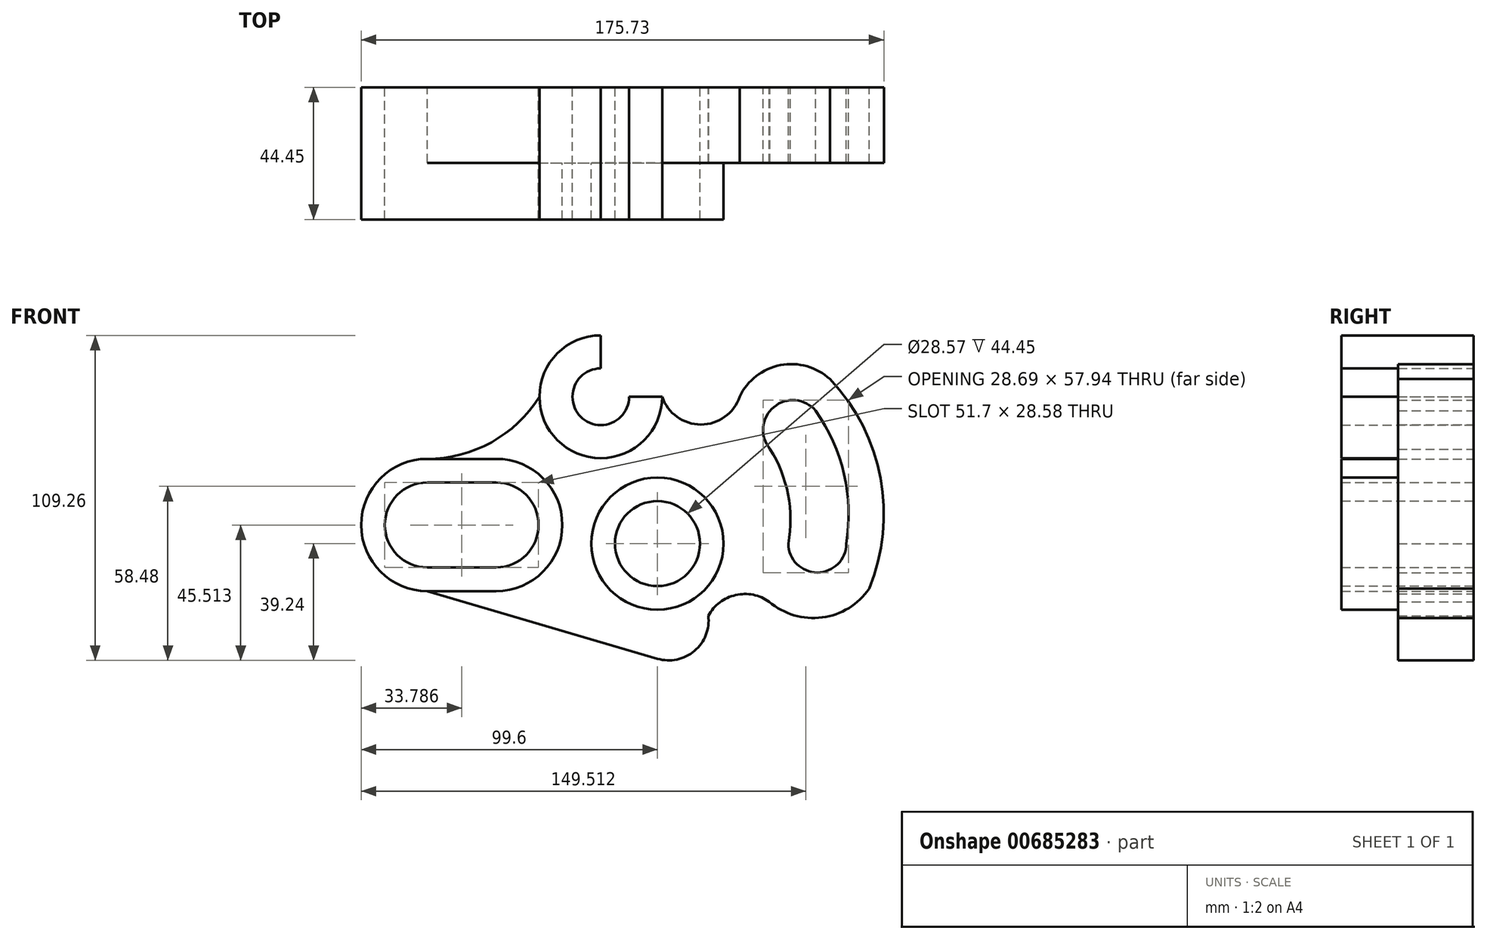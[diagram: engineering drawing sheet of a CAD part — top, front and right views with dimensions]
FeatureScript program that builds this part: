
annotation { "Feature Type Name" : "Feature", "Feature Type Description" : "" }
export const myFeature = defineFeature(function(context is Context, id is Id, definition is map)
    precondition{}
    {
        {
            var Q0;
            Q0=qCreatedBy(makeId("Front.planeOp"),FACE);
            var sketch = newSketch(context, id + "F0", { "sketchPlane" : qUnion([Q0])});
            skLineSegment(sketch, "E0", {"start": v(0, 0) * mm, "end": v(63.5, 0) * mm});
            skCircle(sketch, "E1", {"center": v(0, 0) * mm, "radius": 14.29 * mm});
            skCircle(sketch, "E2", {"center": v(0, 0) * mm, "radius": 22.23 * mm});
            skArc(sketch, "E3", {"start": v(-77.37, 28.5) * mm, "mid": v(-99.6, 6.27) * mm, "end": v(-77.37, -15.95) * mm});
            skLineSegment(sketch, "E4", {"start": v(-77.37, 28.5) * mm, "end": v(-54.2, 28.5) * mm});
            skLineSegment(sketch, "E5", {"start": v(-77.37, -15.95) * mm, "end": v(-54.2, -15.95) * mm});
            skArc(sketch, "E6", {"start": v(-54.2, -15.95) * mm, "mid": v(-31.98, 6.27) * mm, "end": v(-54.2, 28.5) * mm});
            skArc(sketch, "E7", {"start": v(-77.37, 20.56) * mm, "mid": v(-91.66, 6.27) * mm, "end": v(-77.37, -8.01) * mm});
            skArc(sketch, "E8", {"start": v(-54.2, -8.01) * mm, "mid": v(-39.97, 6.27) * mm, "end": v(-54.2, 20.56) * mm});
            skLineSegment(sketch, "E9", {"start": v(-77.37, 20.56) * mm, "end": v(-54.2, 20.56) * mm});
            skLineSegment(sketch, "E10", {"start": v(-77.37, -8.01) * mm, "end": v(-54.2, -8.01) * mm});
            skLineSegment(sketch, "E11", {"start": v(-77.37, -15.95) * mm, "end": v(0, -38.7) * mm});
            skCircle(sketch, "E12", {"center": v(-19.05, 49.38) * mm, "radius": 9.53 * mm});
            skCircle(sketch, "E13", {"center": v(-19.05, 49.38) * mm, "radius": 20.64 * mm});
            skLineSegment(sketch, "E14", {"start": v(-19.05, 87.42) * mm, "end": v(-19.05, 22.5) * mm});
            skArc(sketch, "E15", {"start": v(-77.37, 28.5) * mm, "mid": v(-55.83, 34.07) * mm, "end": v(-39.69, 49.38) * mm});
            skLineSegment(sketch, "E16", {"start": v(0, 0) * mm, "end": v(53.23, 44.67) * mm});
            skArc(sketch, "E17", {"start": v(44.03, 0) * mm, "mid": v(43.92, 16.46) * mm, "end": v(37.87, 31.78) * mm});
            skArc(sketch, "E18", {"start": v(63.5, 0) * mm, "mid": v(62.75, 23.34) * mm, "end": v(53.23, 44.67) * mm});
            skArc(sketch, "E19", {"start": v(53.23, 44.67) * mm, "mid": v(39.1, 45.9) * mm, "end": v(37.87, 31.78) * mm});
            skArc(sketch, "E20", {"start": v(44.03, 0) * mm, "mid": v(53.76, -9.73) * mm, "end": v(63.5, 0) * mm});
            skLineSegment(sketch, "E21", {"start": v(-19.05, 49.38) * mm, "end": v(1.59, 49.38) * mm});
            skArc(sketch, "E22", {"start": v(1.59, 49.38) * mm, "mid": v(14.61, 40.05) * mm, "end": v(27.63, 49.38) * mm});
            skArc(sketch, "E23", {"start": v(58.04, 55.3) * mm, "mid": v(41.34, 60) * mm, "end": v(27.63, 49.38) * mm});
            skArc(sketch, "E24", {"start": v(71.2, -15.16) * mm, "mid": v(75, 22.01) * mm, "end": v(58.04, 55.3) * mm});
            skArc(sketch, "E25", {"start": v(37.57, -19.54) * mm, "mid": v(55.36, -24.83) * mm, "end": v(71.2, -15.16) * mm});
            skArc(sketch, "E26", {"start": v(37.57, -19.54) * mm, "mid": v(26.3, -17.3) * mm, "end": v(17.1, -24.22) * mm});
            skArc(sketch, "E27", {"start": v(0, -38.7) * mm, "mid": v(12.45, -36.07) * mm, "end": v(17.1, -24.22) * mm});
            skSolve(sketch);
        }
        {
            var Q0;
            Q0=makeQuery(id+"F0.imprint","IMPRINT",FACE,{"disambiguationData":[TD([[makeQuery(id+"F0.imprint","IMPRINT",EDGE,{"derivedFrom":sQuery(id+"F0.wireOp",EDGE,"E4")}),1.0]])]});
            var Q1;
            {var subQ0=sQuery(id+"F0.wireOp",EDGE,"E17");Q1=makeQuery(id+"F0.imprint","IMPRINT",FACE,{"disambiguationData":[TD([[makeQuery(id+"F0.imprint","IMPRINT",EDGE,{"derivedFrom":subQ0}),1.0]])]});}
            extrude(context, id + "F1", {"entities" : qUnion([Q0, Q1]), "depth" : 25.4 * mm, "offsetDistance" : 25.4 * mm});
        }
        {
            var Q0;
            {var subQ0=sQuery(id+"F0.wireOp",EDGE,"E14");var subQ3=sQuery(id+"F0.wireOp",EDGE,"E12");var subQ4=makeQuery(id+"F0.imprint","INTERSECT",VERTEX,{"disambiguationData":[OD(0.0)],"derivedFrom":[subQ3,subQ0]});Q0=makeQuery(id+"F0.imprint","IMPRINT",FACE,{"disambiguationData":[TD([[makeQuery(id+"F0.imprint","IMPRINT",EDGE,{"disambiguationData":[TD([[subQ4,-1.0]])],"derivedFrom":subQ3}),-1.0]])]});}
            var Q1;
            {var subQ0=sQuery(id+"F0.wireOp",EDGE,"E14");var subQ1=sQuery(id+"F0.wireOp",EDGE,"E12");var subQ2=makeQuery(id+"F0.imprint","INTERSECT",VERTEX,{"disambiguationData":[OD(0.0)],"derivedFrom":[subQ1,subQ0]});Q1=makeQuery(id+"F0.imprint","IMPRINT",FACE,{"disambiguationData":[TD([[makeQuery(id+"F0.imprint","IMPRINT",EDGE,{"disambiguationData":[TD([[subQ2,1.0]])],"derivedFrom":subQ1}),-1.0]])]});}
            var Q2;
            {var subQ0=sQuery(id+"F0.wireOp",EDGE,"E21");var subQ1=sQuery(id+"F0.wireOp",EDGE,"E12");var subQ2=makeQuery(id+"F0.imprint","INTERSECT",VERTEX,{"derivedFrom":[subQ1,subQ0]});Q2=makeQuery(id+"F0.imprint","IMPRINT",FACE,{"disambiguationData":[TD([[makeQuery(id+"F0.imprint","IMPRINT",EDGE,{"disambiguationData":[TD([[subQ2,1.0]])],"derivedFrom":subQ1}),-1.0]])]});}
            var Q3;
            Q3=makeQuery(id+"F0.imprint","IMPRINT",FACE,{"disambiguationData":[TD([[makeQuery(id+"F0.imprint","IMPRINT",EDGE,{"derivedFrom":sQuery(id+"F0.wireOp",EDGE,"E3")}),1.0]])]});
            var Q4;
            {var subQ0=sQuery(id+"F0.wireOp",EDGE,"E1");var subQ1=sQuery(id+"F0.wireOp",EDGE,"E0");var subQ2=makeQuery(id+"F0.imprint","INTERSECT",VERTEX,{"derivedFrom":[subQ1,subQ0]});Q4=makeQuery(id+"F0.imprint","IMPRINT",FACE,{"disambiguationData":[TD([[makeQuery(id+"F0.imprint","IMPRINT",EDGE,{"disambiguationData":[TD([[subQ2,-1.0]])],"derivedFrom":subQ1}),-1.0]])]});}
            var Q5;
            {var subQ0=sQuery(id+"F0.wireOp",EDGE,"E1");var subQ1=sQuery(id+"F0.wireOp",EDGE,"E0");var subQ2=makeQuery(id+"F0.imprint","INTERSECT",VERTEX,{"derivedFrom":[subQ1,subQ0]});Q5=makeQuery(id+"F0.imprint","IMPRINT",FACE,{"disambiguationData":[TD([[makeQuery(id+"F0.imprint","IMPRINT",EDGE,{"disambiguationData":[TD([[subQ2,-1.0]])],"derivedFrom":subQ1}),1.0]])]});}
            extrude(context, id + "F2", {"entities" : qUnion([Q0, Q1, Q2, Q3, Q4, Q5]), "operationType" : NewBodyOperationType.ADD, "depth" : 44.45 * mm, "offsetDistance" : 25.4 * mm});
        }
    });
